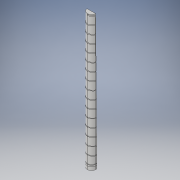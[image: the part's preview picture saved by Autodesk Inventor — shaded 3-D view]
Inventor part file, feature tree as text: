
AUTODESK INVENTOR PART (.ipt)
format: ipt  version: 2018 (Build 220112000, 112)  size: 2,099,712 bytes
history: native  units: in
note: dims shown in document units (in); Inventor stores cm internally (conversion verified against a paired STEP export)
features: sketch x13, extrude x12, plane x7, other x7, reference x3, projected_geometry x3, mirror x2, surface_op x1, loft x1, direct_edit x1
ambient origin geometry x8: Origin, YZ Plane, XZ Plane, XY Plane, X Axis, Y Axis, Z Axis, Center Point
bodies: Solid1 (feature_tree)
feature tree (50):
  extrude  "Extrusion1"  Depth=3.0in
  extrude  "Extrusion2"  Depth=1.0in TaperAngle=0.0deg
  extrude  "Extrusion3"  Depth=3.0in TaperAngle=0.0deg
  extrude  "Extrusion4"  Depth=3.0in TaperAngle=0.0deg
  extrude  "Extrusion5"  Depth=7.25in TaperAngle=0.0deg
  plane  "Work Plane1"
  plane  "Work Plane2"
  mirror  "Mirror1"
  mirror  "Mirror2"
  extrude  "Extrusion6"  Depth=0.25in
  surface_op  "Sculpt1"
  extrude  "Extrusion7"  Depth=2.0in TaperAngle=0.0deg
  extrude  "Extrusion9"  Depth=11.811in TaperAngle=0.0deg
  extrude  "Extrusion10"  TaperAngle=0.0deg  [1 undecoded]
  extrude  "Extrusion13"  Depth=0.3937in
  loft  "Loft1"
  direct_edit  "Direct Edit2"
  extrude  "Extrusion16"  [1 undecoded]
  plane  "Work Plane3"
  plane  "Work Plane4"
  plane  "Work Plane5"
  plane  "Work Plane6"
  plane  "Work Plane7"
  extrude  "Extrusion20"  [1 undecoded]
  sketch  "Sketch1"  dims[d0=1.0in d1=3.0in]
  sketch  "Sketch3"  dims[d2=1.0in d3=0.0in d4=1.0in d5=0.0in]
  sketch  "Sketch4"  dims[d6=1.0in d7=0.0in d8=3.0in d9=0.0in]
  reference  "Reference1"
  sketch  "Sketch5"  dims[d10=0.3in d11=3.0in d12=0.0in]
  reference  "Reference2"
  reference  "Reference3"
  sketch  "Sketch6"  dims[d13=7.25in d14=0.0in d15=7.25in d16=0.0in]
  sketch  "Sketch7"  dims[d19=0.25in d20=0.25in]
  projected_geometry  "Projected Loop1"
  sketch  "Sketch8"  dims[d21=2.0in d22=0.0in d23=2.0in d24=0.0in]
  sketch  "Sketch10"  dims[d36=0.0148in d37=11.811in d38=0.0in]
  sketch  "Sketch11"  dims[d39=0.0074in d40=0.0in d41=90.0deg]
  sketch  "Sketch14"  dims[d42=0.0in d43=90.0deg d44=0.3937in d45=0.374in d46=0.374in]
  sketch  "Sketch15"  dims[d52=0.1969in d53=0.0in d66=-0.3937in]
  projected_geometry  "Projected Loop2"
  other  "Edges1"
  sketch  "Sketch18"  dims[d69=3.937in d70=0.0in]
  projected_geometry  "Projected Loop3"
  sketch  "Sketch24"
  other  "<userpath>\Desktop\spring jig.iam"
  other  "spring jig.iam"
  other  "AR-15 GI Magazine Spring Uncompressed:1"
  other  "Composite1"
  other  "Srf1"
  other  "Scale2"
note: 3 required parameter values undecoded (feature->parameter linkage not recoverable at this tier; creation-order binding heuristic only, values carry confidence <= 0.55)
